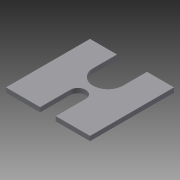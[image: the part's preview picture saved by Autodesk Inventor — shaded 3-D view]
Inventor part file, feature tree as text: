
AUTODESK INVENTOR PART (.ipt)
format: ipt  version: 2013 (Build 170138000, 138)  size: 89,600 bytes
history: native  units: in
note: dims shown in document units (in); Inventor stores cm internally (conversion verified against a paired STEP export)
features: extrude x1, mirror x1, sketch x1
ambient origin geometry x8: Origin, YZ Plane, XZ Plane, XY Plane, X Axis, Y Axis, Z Axis, Center Point
bodies: Solid1 (feature_tree)
feature tree (3):
  extrude  "Extrusion1"  Depth=1.25in
  mirror  "Mirror1"
  sketch  "Sketch1"  dims[d2=0.325in d8=1.25in d9=3.5in d11=1.75in d12=0.1875in d13=0.0in d14=1.0in d15=0.625in]
